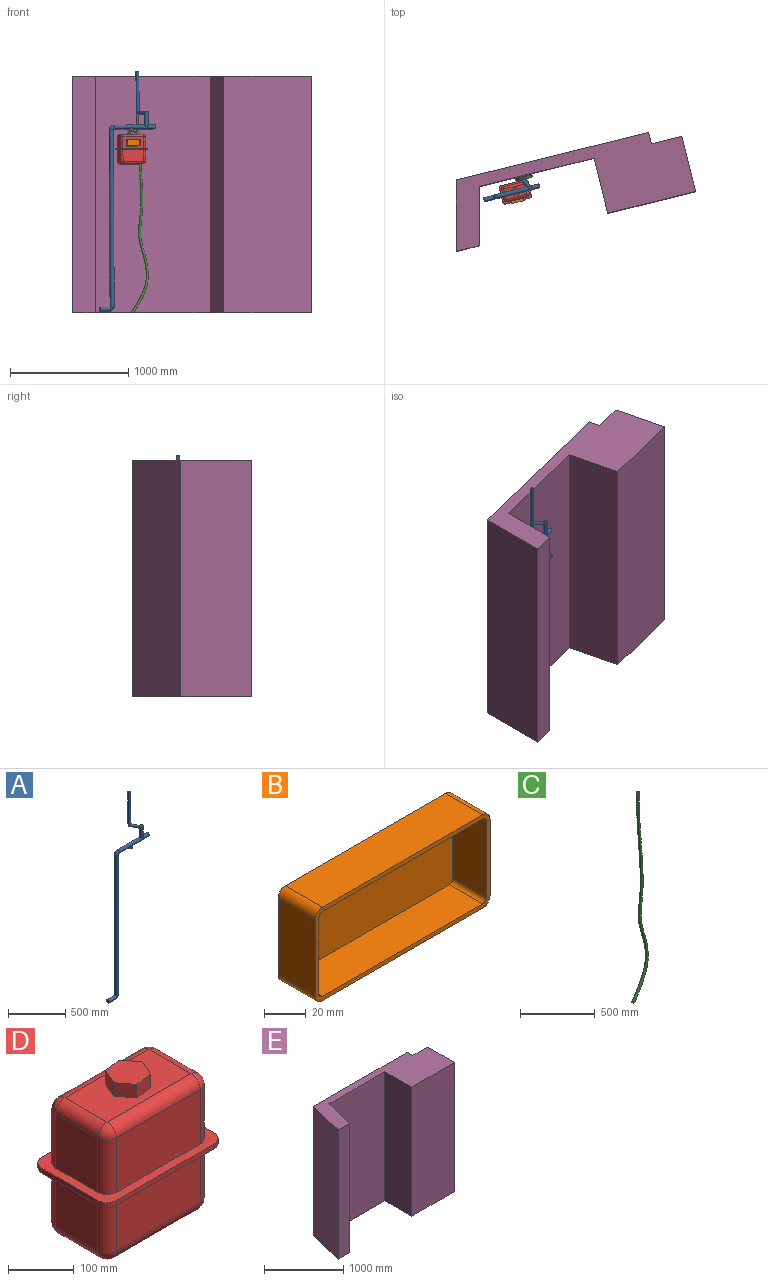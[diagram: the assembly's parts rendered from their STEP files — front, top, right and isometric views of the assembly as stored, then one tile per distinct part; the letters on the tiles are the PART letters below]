
ASSEMBLY  parts=5 mates=5
PART A: 17 faces, bbox 490.2x130.2x2030.6 mm
  f0: cylinder r=12.5mm len=340mm, axis (0,0,-1), area 26703.5mm2, adj f1,f3,f16
  f1: plane 25.24x25.24mm, normal (0,0,-1), area 447.8mm2, adj f0,f2,f3
  f2: cone r=12.65mm half-angle=86.1deg, axis (0.45,-0.89,0), area 503.9mm2, adj f1,f3
  f3: cylinder r=12.65mm len=111.31mm, axis (-0.45,0.89,0), area 7730.9mm2, adj f0,f1,f2,f4,f5,f15
  f4: cone r=12.65mm half-angle=86.1deg, axis (0.45,-0.89,0), area 0mm2, adj f3,f15
  f5: cylinder r=17.5mm len=130mm, axis (0,0,-1), area 12518.7mm2, adj f3,f6,f15
  f6: cylinder r=17.5mm len=365mm, axis (-1,0,0), area 37683.8mm2, adj f5,f7,f12,f13
  f7: torus R=20mm, axis (0,-1,0), area 3454.4mm2, adj f6,f8
  f8: cylinder r=17.5mm len=1502.5mm, axis (0,0,-1), area 165208.5mm2, adj f7,f9
  f9: torus R=17.5mm, axis (0,1,0), area 3022.6mm2, adj f8,f10
  f10: cylinder r=17.5mm len=87.5mm, axis (-1,0,0), area 9621.1mm2, adj f9,f11
  f11: plane 35x35mm, normal (-1,0,0), area 962.1mm2, adj f10
  f12: plane 35x35mm, normal (1,0,0), area 962.1mm2, adj f6
  f13: cylinder r=17.5mm len=38mm, axis (0,0,-1), area 2953.3mm2, adj f6,f14
  f14: plane 35x35mm, normal (0,0,-1), area 962.1mm2, adj f13
  f15: plane 35.24x35.24mm, normal (0,0,1), area 901.5mm2, adj f3,f4,f5
  f16: plane 25x25mm, normal (0,0,1), area 490.9mm2, adj f0
PART B: 19 faces, bbox 117.8x25x54.5 mm
  f0: plane 107.83x25mm, normal (0,0,-1), area 2695.6mm2, adj f1,f7,f8,f9
  f1: cylinder r=5mm len=25mm, axis (0,1,0), area 196.3mm2, adj f0,f2,f8,f9
  f2: plane 44.47x25mm, normal (1,0,0), area 1111.7mm2, adj f1,f3,f8,f9
  f3: cylinder r=5mm len=25mm, axis (0,1,0), area 196.3mm2, adj f2,f4,f8,f9
  f4: plane 107.83x25mm, normal (0,0,1), area 2695.6mm2, adj f3,f5,f8,f9
  f5: cylinder r=5mm len=25mm, axis (0,1,0), area 196.3mm2, adj f4,f6,f8,f9
  f6: plane 44.47x25mm, normal (-1,0,0), area 1111.7mm2, adj f5,f7,f8,f9
  f7: cylinder r=5mm len=25mm, axis (0,1,0), area 196.3mm2, adj f0,f6,f8,f9
  f8: plane 117.83x54.47mm, normal (0,-1,0), area 820.4mm2, adj f0,f1,f2,f3,f4,f5,f6,f7
  f9: plane 117.83x54.47mm, normal (0,1,0), area 6396.3mm2, adj f0,f1,f2,f3,f4,f5,f6,f7
  f10: plane 107.83x22.5mm, normal (0,0,1), area 2426.1mm2, adj f8,f11,f17,f18
  f11: cylinder r=2.5mm len=22.5mm, axis (0,1,0), area 88.4mm2, adj f8,f10,f12,f18
  f12: plane 44.47x22.5mm, normal (-1,0,0), area 1000.5mm2, adj f8,f11,f13,f18
  f13: cylinder r=2.5mm len=22.5mm, axis (0,1,0), area 88.4mm2, adj f8,f12,f14,f18
  f14: plane 107.83x22.5mm, normal (0,0,-1), area 2426.1mm2, adj f8,f13,f15,f18
  f15: cylinder r=2.5mm len=22.5mm, axis (0,1,0), area 88.4mm2, adj f8,f14,f16,f18
  f16: plane 44.47x22.5mm, normal (1,0,0), area 1000.5mm2, adj f8,f15,f17,f18
  f17: cylinder r=2.5mm len=22.5mm, axis (0,1,0), area 88.4mm2, adj f8,f10,f16,f18
  f18: plane 112.83x49.47mm, normal (0,-1,0), area 5575.9mm2, adj f10,f11,f12,f13,f14,f15,f16,f17
PART C: 3 faces, bbox 148.7x40x1704.3 mm
  f0: plane 20x20mm, normal (0,0,-1), area 314.2mm2, adj f2
  f1: plane 20x18.04mm, normal (-0.43,0,0.9), area 314.2mm2, adj f2
  f2: bspline ~1704.32x148.68mm, area 102473.3mm2, adj f0,f1
PART D: 51 faces, bbox 250x160x275 mm
  f0: plane 180x90mm, normal (0,0,1), area 13082.3mm2, adj f16,f17,f18,f19,f44,f45,f46,f47
  f1: plane 180x100.56mm, normal (0,1,0), area 18100.5mm2, adj f10,f33,f37,f39
  f2: plane 100.56x90mm, normal (-1,0,0), area 9050.3mm2, adj f10,f30,f36,f39
  f3: plane 100.56x90mm, normal (1,0,0), area 9050.3mm2, adj f10,f28,f32,f33
  f4: plane 180x100.56mm, normal (0,-1,0), area 18100.5mm2, adj f10,f28,f30,f31
  f5: plane 180x100.56mm, normal (0,1,0), area 18100.5mm2, adj f12,f16,f20,f22
  f6: plane 100.56x90mm, normal (-1,0,0), area 9050.3mm2, adj f12,f17,f20,f26
  f7: plane 180x100.56mm, normal (0,-1,0), area 18100.5mm2, adj f12,f19,f24,f26
  f8: plane 100.56x90mm, normal (1,0,0), area 9050.3mm2, adj f12,f18,f22,f24
  f9: plane 180x90mm, normal (0,0,-1), area 16200mm2, adj f31,f32,f36,f37
  f10: plane 250x160mm, normal (0,0,-1), area 11400mm2, adj f1,f2,f3,f4,f11,f13,f14,f15
  f11: plane 120x8.88mm, normal (1,0,0), area 1066mm2, adj f10,f12,f40,f42
  f12: plane 250x160mm, normal (0,0,1), area 11400mm2, adj f5,f6,f7,f8,f11,f13,f14,f15
  f13: plane 120x8.88mm, normal (-1,0,0), area 1066mm2, adj f10,f12,f41,f43
  f14: plane 210x8.88mm, normal (0,-1,0), area 1865.4mm2, adj f10,f12,f42,f43
  f15: plane 210x8.88mm, normal (0,1,0), area 1865.4mm2, adj f10,f12,f40,f41
  f16: cylinder r=20mm len=180mm, axis (-1,0,0), area 5654.9mm2, adj f0,f5,f21,f23
  f17: cylinder r=20mm len=90mm, axis (0,-1,0), area 2827.4mm2, adj f0,f6,f21,f27
  f18: cylinder r=20mm len=90mm, axis (0,1,0), area 2827.4mm2, adj f0,f8,f23,f25
  f19: cylinder r=20mm len=180mm, axis (1,0,0), area 5654.9mm2, adj f0,f7,f25,f27
  f20: cylinder r=20mm len=100.56mm, axis (0,0,-1), area 3159.1mm2, adj f5,f6,f12,f21
  f21: sphere r=20mm, area 628.3mm2, adj f16,f17,f20
  f22: cylinder r=20mm len=100.56mm, axis (0,0,1), area 3159.1mm2, adj f5,f8,f12,f23
  f23: sphere r=20mm, area 628.3mm2, adj f16,f18,f22
  f24: cylinder r=20mm len=100.56mm, axis (0,0,-1), area 3159.1mm2, adj f7,f8,f12,f25
  f25: sphere r=20mm, area 628.3mm2, adj f18,f19,f24
  f26: cylinder r=20mm len=100.56mm, axis (0,0,1), area 3159.1mm2, adj f6,f7,f12,f27
  f27: sphere r=20mm, area 628.3mm2, adj f17,f19,f26
  f28: cylinder r=20mm len=100.56mm, axis (0,0,-1), area 3159.1mm2, adj f3,f4,f10,f29
  f29: sphere r=20mm, area 628.3mm2, adj f28,f31,f32
  f30: cylinder r=20mm len=100.56mm, axis (0,0,1), area 3159.1mm2, adj f2,f4,f10,f34
  f31: cylinder r=20mm len=180mm, axis (-1,0,0), area 5654.9mm2, adj f4,f9,f29,f34
  f32: cylinder r=20mm len=90mm, axis (0,-1,0), area 2827.4mm2, adj f3,f9,f29,f35
  f33: cylinder r=20mm len=100.56mm, axis (0,0,1), area 3159.1mm2, adj f1,f3,f10,f35
  f34: sphere r=20mm, area 628.3mm2, adj f30,f31,f36
  f35: sphere r=20mm, area 628.3mm2, adj f32,f33,f37
  f36: cylinder r=20mm len=90mm, axis (0,1,0), area 2827.4mm2, adj f2,f9,f34,f38
  f37: cylinder r=20mm len=180mm, axis (1,0,0), area 5654.9mm2, adj f1,f9,f35,f38
  f38: sphere r=20mm, area 628.3mm2, adj f36,f37,f39
  f39: cylinder r=20mm len=100.56mm, axis (0,0,-1), area 3159.1mm2, adj f1,f2,f10,f38
  f40: cylinder r=20mm len=20mm, axis (0,0,1), area 279.1mm2, adj f10,f11,f12,f15
  f41: cylinder r=20mm len=20mm, axis (0,0,-1), area 279.1mm2, adj f10,f12,f13,f15
  f42: cylinder r=20mm len=20mm, axis (0,0,-1), area 279.1mm2, adj f10,f11,f12,f14
  f43: cylinder r=20mm len=20mm, axis (0,0,1), area 279.1mm2, adj f10,f12,f13,f14
  f44: plane 34.35x25mm, normal (0.13,-0.99,0), area 866mm2, adj f0,f45,f49,f50
  f45: plane 32x25mm, normal (0.92,-0.38,0), area 866mm2, adj f0,f44,f46,f50
  f46: plane 27.49x25mm, normal (0.79,0.61,0), area 866mm2, adj f0,f45,f47,f50
  f47: plane 34.35x25mm, normal (-0.13,0.99,0), area 866mm2, adj f0,f46,f48,f50
  f48: plane 32x25mm, normal (-0.92,0.38,0), area 866mm2, adj f0,f47,f49,f50
  f49: plane 27.49x25mm, normal (-0.79,-0.61,0), area 866mm2, adj f0,f44,f48,f50
  f50: plane 68.69x63.99mm, normal (0,0,1), area 3117.7mm2, adj f44,f45,f46,f47,f48,f49
PART E: 12 faces, bbox 2085.7x585.4x2000 mm
  f0: plane 2000x1000mm, normal (0,-1,0), area 2000000mm2, adj f1,f6,f7,f9
  f1: plane 2000x485.39mm, normal (0.97,-0.24,0), area 1000000mm2, adj f0,f5,f6,f7
  f2: plane 2000x100mm, normal (1,0,0), area 200000mm2, adj f3,f6,f7,f8
  f3: plane 2000x1675.28mm, normal (0,1,0), area 3350554.9mm2, adj f2,f4,f6,f7
  f4: plane 2000x585.39mm, normal (-0.97,0.24,0), area 1206021.4mm2, adj f3,f5,f6,f7
  f5: plane 2000x200mm, normal (0,-1,0), area 400000mm2, adj f1,f4,f6,f7
  f6: plane 2085.71x585.39mm, normal (0,0,1), area 633383.9mm2, adj f0,f1,f2,f3,f4,f5,f8,f9
  f7: plane 2085.71x585.39mm, normal (0,0,-1), area 633383.9mm2, adj f0,f1,f2,f3,f4,f5,f8,f9
  f8: plane 2000x265.71mm, normal (0,1,0), area 531428.2mm2, adj f2,f6,f7,f11
  f9: plane 2000x480mm, normal (-1,0,0), area 960000mm2, adj f0,f6,f7,f10
  f10: plane 2000x765.71mm, normal (0,-1,0), area 1531428.2mm2, adj f6,f7,f9,f11
  f11: plane 2000x480mm, normal (1,0,0), area 960000mm2, adj f6,f7,f8,f10
PLACE A rot(axis=(0,-0.02,1),13.9deg) t=(-554.42,-1316.48,421.26)mm
PLACE B rot(axis=(0,-0.02,1),13.9deg) t=(-558.75,-1317.55,396.52)mm
PLACE C rot(axis=(0,0,1),13.9deg) t=(-742.07,-1311.37,-1084.82)mm
PLACE D rot(axis=(0,-0.02,1),13.9deg) t=(-554.42,-1316.48,421.26)mm
PLACE E rot(axis=(0,0,1),13.9deg) t=(-736.8,-1308,-1084.82)mm fixed
MATE fastened C.f0 <-> E.f7  axis (0,0,-1) through (-422.07,-1247.71,-1084.82)mm
MATE ball C.f1 <-> A.f0  axis (-0.42,-0.1,0.9) through (-379.29,-1237.13,615.18)mm
MATE fastened D.f7 <-> B.f9  axis (0.24,-0.97,0) through (-416.1,-1416.2,351.52)mm
MATE fastened D.f50 <-> A.f13  axis (0,0,1) through (-432.15,-1353.21,446.8)mm
MATE parallel D.f4 <-> E.f0  axis (0.24,-0.97,0) through (-415.59,-1416.07,242.08)mm
